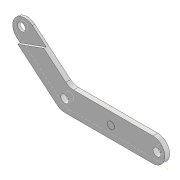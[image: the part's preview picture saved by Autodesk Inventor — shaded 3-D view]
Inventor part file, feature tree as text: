
AUTODESK INVENTOR PART (.ipt)
format: ipt  version: 2021 (Build 250183000, 183)  size: 151,552 bytes
history: native  units: mm
features: sketch x6, extrude x5, projected_geometry x1
ambient origin geometry x8: Origin, YZ Plane, XZ Plane, XY Plane, X Axis, Y Axis, Z Axis, Center Point
bodies: Solid1 (feature_tree)
feature tree (12):
  extrude  "Extrusion1"  Depth=30.0mm
  sketch  "Sketch2"  dims[d3=8.726646mm d4=120.0mm]
  extrude  "Extrusion2"  Depth=120.0mm
  extrude  "Extrusion3"  Depth=10.0mm
  extrude  "Extrusion4"  Depth=10.0mm
  extrude  "Extrusion5"  Depth=15.0mm
  sketch  "Sketch1"  dims[d0=30.0mm d2=30.0mm]
  sketch  "Sketch3"  dims[d5=90.0mm d6=10.0mm]
  projected_geometry  "Projected Loop1"
  sketch  "Sketch4"  dims[d7=10.0mm d8=10.0mm]
  sketch  "Sketch5"  dims[d9=10.0mm d10=15.0mm]
  sketch  "Sketch6"  dims[d11=3.0mm d12=0.0mm d13=10.0mm d14=15.0mm d15=15.0mm d16=60.0deg d17=36.0mm d18=3.0mm d19=0.0mm d20=12.0mm d21=0.0mm d22=115.459554mm d23=57.729777mm d24=0.1mm d25=0.0mm d26=0.1mm d27=0.0mm d28=5.0mm]
